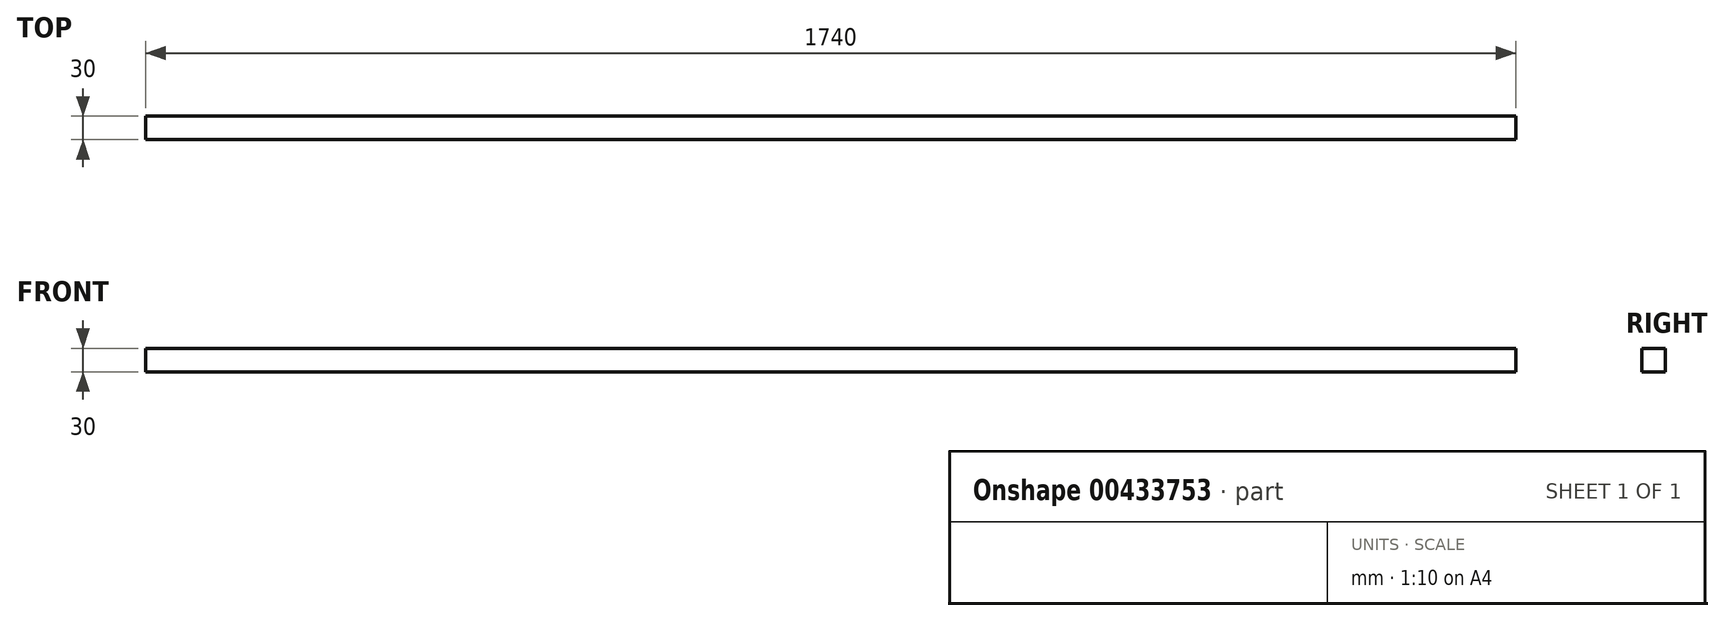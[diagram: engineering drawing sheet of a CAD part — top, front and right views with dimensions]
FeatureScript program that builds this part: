
annotation { "Feature Type Name" : "Feature", "Feature Type Description" : "" }
export const myFeature = defineFeature(function(context is Context, id is Id, definition is map)
    precondition{}
    {
        {
            var Q0;
            Q0=qCreatedBy(makeId("Front.planeOp"),FACE);
            var sketch = newSketch(context, id + "F0", { "sketchPlane" : qUnion([Q0])});
            skLineSegment(sketch, "E0.bottom", {"start": v(-167.06, 30) * mm, "end": v(1572.94, 30) * mm});
            skLineSegment(sketch, "E0.top", {"start": v(-167.06, 0) * mm, "end": v(1572.94, 0) * mm});
            skLineSegment(sketch, "E0.left", {"start": v(-167.06, 30) * mm, "end": v(-167.06, 0) * mm});
            skLineSegment(sketch, "E0.right", {"start": v(1572.94, 30) * mm, "end": v(1572.94, 0) * mm});
            skSolve(sketch);
        }
        {
            var Q0;
            Q0 = qSketchRegion(id + "F0", true);
            extrude(context, id + "F1", {"entities" : qUnion([Q0]), "depth" : 30 * mm, "offsetDistance" : 25 * mm});
        }
    });
